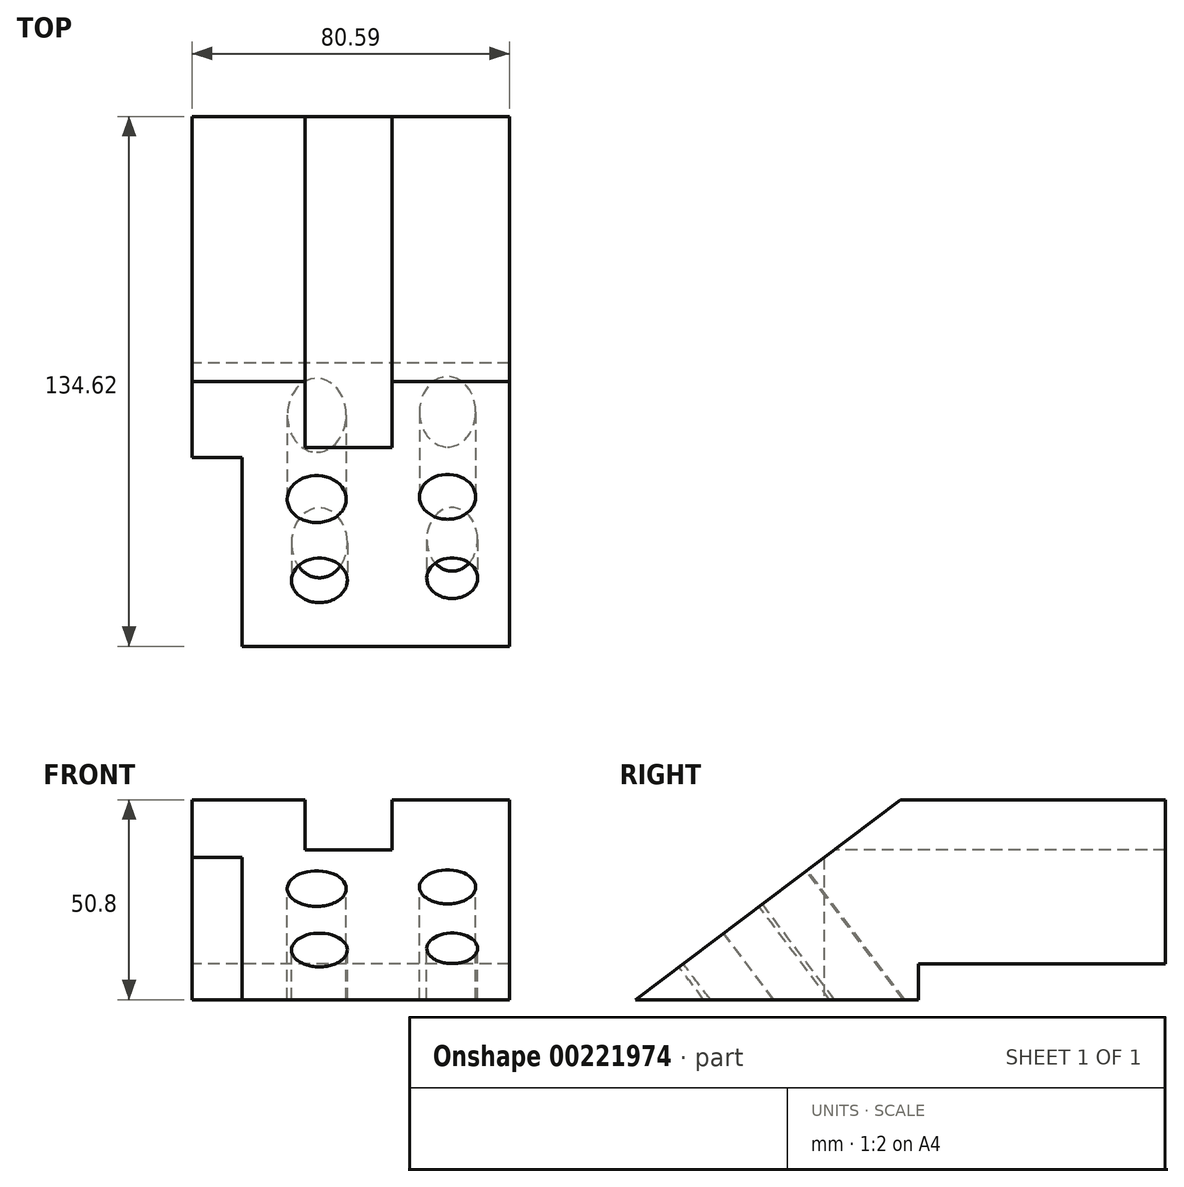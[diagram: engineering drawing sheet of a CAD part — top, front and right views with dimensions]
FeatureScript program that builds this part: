
annotation { "Feature Type Name" : "Feature", "Feature Type Description" : "" }
export const myFeature = defineFeature(function(context is Context, id is Id, definition is map)
    precondition{}
    {
        {
            var Q0;
            Q0=qCreatedBy(makeId("Top.planeOp"),FACE);
            var sketch = newSketch(context, id + "F0", { "sketchPlane" : qUnion([Q0])});
            skLineSegment(sketch, "E0.bottom", {"start": v(-39.72, 67.54) * mm, "end": v(40.87, 67.54) * mm});
            skLineSegment(sketch, "E0.top", {"start": v(-39.72, -67.08) * mm, "end": v(40.87, -67.08) * mm});
            skLineSegment(sketch, "E0.left", {"start": v(-39.72, 67.54) * mm, "end": v(-39.72, -67.08) * mm});
            skLineSegment(sketch, "E0.right", {"start": v(40.87, 67.54) * mm, "end": v(40.87, -67.08) * mm});
            skSolve(sketch);
        }
        {
            var Q0;
            Q0 = qSketchRegion(id + "F0", true);
            extrude(context, id + "F1", {"entities" : qUnion([Q0]), "depth" : 50.8 * mm});
        }
        {
            var Q0;
            Q0=makeQuery(id+"F1.opExtrude","SWEPT_FACE",FACE,{"disambiguationData":[OSD([sQuery(id+"F0.wireOp",EDGE,"E0.left")])]});
            var sketch = newSketch(context, id + "F2", { "sketchPlane" : qUnion([Q0])});
            skLineSegment(sketch, "E1", {"start": v(-0.23, 50.8) * mm, "end": v(67.08, 0) * mm});
            skLineSegment(sketch, "E2", {"start": v(67.08, 0) * mm, "end": v(67.08, 50.8) * mm});
            skLineSegment(sketch, "E3", {"start": v(67.08, 50.8) * mm, "end": v(-0.23, 50.8) * mm});
            skSolve(sketch);
        }
        {
            var Q0;
            Q0=makeQuery(id+"F1.opExtrude","CAP_FACE",FACE,{"disambiguationData":[OSD([sQuery(id+"F0.wireOp",EDGE,"E0.bottom"),sQuery(id+"F0.wireOp",EDGE,"E0.top"),sQuery(id+"F0.wireOp",EDGE,"E0.left"),sQuery(id+"F0.wireOp",EDGE,"E0.right")])],"isStart":false});
            var sketch = newSketch(context, id + "F3", { "sketchPlane" : qUnion([Q0])});
            skLineSegment(sketch, "E4.bottom", {"start": v(-11.08, 67.54) * mm, "end": v(11.08, 67.54) * mm});
            skLineSegment(sketch, "E4.top", {"start": v(-11.08, -67.08) * mm, "end": v(11.08, -67.08) * mm});
            skLineSegment(sketch, "E4.left", {"start": v(-11.08, 67.54) * mm, "end": v(-11.08, -67.08) * mm});
            skLineSegment(sketch, "E4.right", {"start": v(11.08, 67.54) * mm, "end": v(11.08, -67.08) * mm});
            skSolve(sketch);
        }
        {
            var Q0;
            Q0 = qSketchRegion(id + "F3", true);
            extrude(context, id + "F4", {"entities" : qUnion([Q0]), "operationType" : NewBodyOperationType.REMOVE, "oppositeDirection" : true, "depth" : 12.7 * mm});
        }
        {
            var Q0;
            Q0 = qSketchRegion(id + "F2", true);
            extrude(context, id + "F5", {"entities" : qUnion([Q0]), "operationType" : NewBodyOperationType.REMOVE, "endBound" : BoundingType.THROUGH_ALL, "oppositeDirection" : true, "depth" : 25.4 * mm});
        }
        {
            var Q0;
            Q0=makeQuery(id+"F5.boolean.opBoolean","COPY",FACE,{"derivedFrom":makeQuery(id+"F5.opExtrude","SWEPT_FACE",FACE,{"disambiguationData":[OSD([sQuery(id+"F2.wireOp",EDGE,"E1")])]})});
            var sketch = newSketch(context, id + "F6", { "sketchPlane" : qUnion([Q0])});
            skCircle(sketch, "E5", {"center": v(-8.08, -6.7) * mm, "radius": 7.5 * mm});
            skSolve(sketch);
        }
        {
            var Q0;
            Q0 = qSketchRegion(id + "F6", true);
            extrude(context, id + "F7", {"entities" : qUnion([Q0]), "operationType" : NewBodyOperationType.REMOVE, "endBound" : BoundingType.THROUGH_ALL, "oppositeDirection" : true, "depth" : 50.8 * mm});
        }
        {
            var Q0;
            Q0=makeQuery(id+"F5.boolean.opBoolean","COPY",FACE,{"derivedFrom":makeQuery(id+"F5.opExtrude","SWEPT_FACE",FACE,{"disambiguationData":[OSD([sQuery(id+"F2.wireOp",EDGE,"E1")])]})});
            var sketch = newSketch(context, id + "F8", { "sketchPlane" : qUnion([Q0])});
            skCircle(sketch, "E6", {"center": v(-7.39, -32.58) * mm, "radius": 7.1 * mm});
            skSolve(sketch);
        }
        {
            var Q0;
            Q0 = qSketchRegion(id + "F8", true);
            extrude(context, id + "F9", {"entities" : qUnion([Q0]), "operationType" : NewBodyOperationType.REMOVE, "endBound" : BoundingType.THROUGH_ALL, "oppositeDirection" : true, "depth" : 25.4 * mm});
        }
        {
            var Q0;
            Q0=makeQuery(id+"F5.boolean.opBoolean","COPY",FACE,{"derivedFrom":makeQuery(id+"F5.opExtrude","SWEPT_FACE",FACE,{"disambiguationData":[OSD([sQuery(id+"F2.wireOp",EDGE,"E1")])]})});
            var sketch = newSketch(context, id + "F10", { "sketchPlane" : qUnion([Q0])});
            skCircle(sketch, "E7", {"center": v(25.17, -6) * mm, "radius": 7.13 * mm});
            skSolve(sketch);
        }
        {
            var Q0;
            Q0 = qSketchRegion(id + "F10", true);
            extrude(context, id + "F11", {"entities" : qUnion([Q0]), "operationType" : NewBodyOperationType.REMOVE, "endBound" : BoundingType.THROUGH_ALL, "oppositeDirection" : true, "depth" : 25.4 * mm});
        }
        {
            var Q0;
            Q0=makeQuery(id+"F5.boolean.opBoolean","COPY",FACE,{"derivedFrom":makeQuery(id+"F5.opExtrude","SWEPT_FACE",FACE,{"disambiguationData":[OSD([sQuery(id+"F2.wireOp",EDGE,"E1")])]})});
            var sketch = newSketch(context, id + "F12", { "sketchPlane" : qUnion([Q0])});
            skCircle(sketch, "E8", {"center": v(26.32, -31.88) * mm, "radius": 6.45 * mm});
            skSolve(sketch);
        }
        {
            var Q0;
            Q0 = qSketchRegion(id + "F12", true);
            extrude(context, id + "F13", {"entities" : qUnion([Q0]), "operationType" : NewBodyOperationType.REMOVE, "endBound" : BoundingType.THROUGH_ALL, "oppositeDirection" : true, "depth" : 25.4 * mm});
        }
        {
            var Q0;
            Q0=makeQuery(id+"F1.opExtrude","SWEPT_FACE",FACE,{"disambiguationData":[OSD([sQuery(id+"F0.wireOp",EDGE,"E0.left")])]});
            var sketch = newSketch(context, id + "F14", { "sketchPlane" : qUnion([Q0])});
            skLineSegment(sketch, "E9", {"start": v(19.18, 36.15) * mm, "end": v(19.18, 0) * mm});
            skLineSegment(sketch, "E10", {"start": v(19.18, 0) * mm, "end": v(67.08, 0) * mm});
            skLineSegment(sketch, "E11", {"start": v(67.08, 0) * mm, "end": v(19.18, 36.15) * mm});
            skSolve(sketch);
        }
        {
            var Q0;
            Q0 = qSketchRegion(id + "F14", true);
            extrude(context, id + "F15", {"entities" : qUnion([Q0]), "operationType" : NewBodyOperationType.REMOVE, "oppositeDirection" : true, "depth" : 12.7 * mm});
        }
        {
            var Q0;
            Q0=makeQuery(id+"F1.opExtrude","SWEPT_FACE",FACE,{"disambiguationData":[OSD([sQuery(id+"F0.wireOp",EDGE,"E0.left")])]});
            var sketch = newSketch(context, id + "F16", { "sketchPlane" : qUnion([Q0])});
            skLineSegment(sketch, "E12.bottom", {"start": v(-4.85, 0) * mm, "end": v(-67.54, 0) * mm});
            skLineSegment(sketch, "E12.top", {"start": v(-4.85, 9.05) * mm, "end": v(-67.54, 9.05) * mm});
            skLineSegment(sketch, "E12.left", {"start": v(-4.85, 0) * mm, "end": v(-4.85, 9.05) * mm});
            skLineSegment(sketch, "E12.right", {"start": v(-67.54, 0) * mm, "end": v(-67.54, 9.05) * mm});
            skSolve(sketch);
        }
        {
            var Q0;
            Q0 = qSketchRegion(id + "F16", true);
            extrude(context, id + "F17", {"entities" : qUnion([Q0]), "operationType" : NewBodyOperationType.REMOVE, "endBound" : BoundingType.THROUGH_ALL, "oppositeDirection" : true, "depth" : 25.4 * mm});
        }
    });
